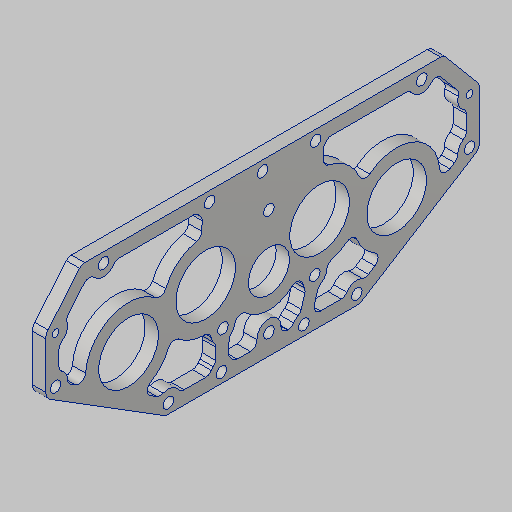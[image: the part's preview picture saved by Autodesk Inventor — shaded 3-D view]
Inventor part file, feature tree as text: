
AUTODESK INVENTOR PART (.ipt)
format: ipt  version: 2023.5 (Build 275446000, 446)  size: 472,064 bytes
history: native  units: in
note: dims shown in document units (in); Inventor stores cm internally (conversion verified against a paired STEP export)
features: sketch x3, hole x3, extrude x2, mirror x2, fillet x1, projected_geometry x1
ambient origin geometry x8: Origin, YZ Plane, XZ Plane, XY Plane, X Axis, Y Axis, Z Axis, Center Point
bodies: Solid1 (feature_tree)
feature tree (12):
  sketch  "Sketch1"  dims[d0=0.125in d1=28.0in]
  sketch  "Sketch3"  dims[d2=2.0in d3=1.0in]
  extrude  "Extrusion1"  Depth=0.125in
  hole  "Mount Holes"  [1 undecoded]
  hole  "Motor Mount"  [1 undecoded]
  mirror  "Mirror1"
  hole  "Hole3"  [1 undecoded]
  mirror  "Mirror2"
  extrude  "Extrusion2"  Depth=0.125in
  fillet  "Fillet2"  Radius=1.0in
  sketch  "Sketch5"  dims[d4=5.5in d5=3.0in d6=1.0in d7=32.0in d8=1.0in d9=0.375in d10=14.0in d11=0.812in d12=0.438in d13=0.3in d23=2.63in d24=2.0in d30=2.256in d31=0.5in d32=2.0in d33=1.0in d34=2.0in d35=0.5in d36=2.0in d37=2.4in d38=1.5in d39=1.375in d40=0.375in d41=1.125in d42=1.125in d43=2.3622in d45=360.0deg d47=2.0in d48=1.0in d49=0.875in d50=0.3in d51=1.0in d52=0.75in d55=0.8933in d57=0.25in d58=0.0in d59=0.201in d60=0.75in d61=0.385in d62=0.25in d63=0.5635in d64=1.0in d65=0.8108in d66=0.775in d68=1.125in d69=1.5in d70=0.201in d71=0.75in d72=0.375in d73=0.25in d74=0.5635in d75=1.0in d76=0.8108in d77=0.13in d78=0.328in d79=0.375in d80=0.25in d81=0.5635in d82=1.0in d83=0.8108in d84=0.25in d85=0.25in d86=0.125in d87=0.125in d88=0.125in d89=0.125in d90=0.125in d91=0.0in d92=0.0in d94=0.125in d95=0.125in d96=0.25in d97=0.125in d98=0.5344in]
  projected_geometry  "Project Cut Edges1"
note: 3 required parameter values undecoded (feature->parameter linkage not recoverable at this tier; creation-order binding heuristic only, values carry confidence <= 0.55)
